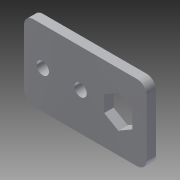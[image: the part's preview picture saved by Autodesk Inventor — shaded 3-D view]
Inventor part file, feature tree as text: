
AUTODESK INVENTOR PART (.ipt)
format: ipt  version: 2014 SP1 (Build 180222100, 222)  size: 101,888 bytes
history: native  units: in
note: dims shown in document units (in); Inventor stores cm internally (conversion verified against a paired STEP export)
features: extrude x1, fillet x1, sketch x1
ambient origin geometry x8: Origin, YZ Plane, XZ Plane, XY Plane, X Axis, Y Axis, Z Axis, Center Point
bodies: Solid1 (feature_tree)
feature tree (3):
  extrude  "Extrusion1"  Depth=1.0in
  fillet  "Fillet1"  Radius=0.163in
  sketch  "Sketch1"  dims[d0=1.625in d1=1.0in d2=0.163in d3=0.5in d4=0.25in d5=1.0in d6=0.375in d7=0.5in d8=0.125in d9=0.0in d10=0.125in d11=0.7874in d13=0.5in d14=0.3937in d16=1.0in]
